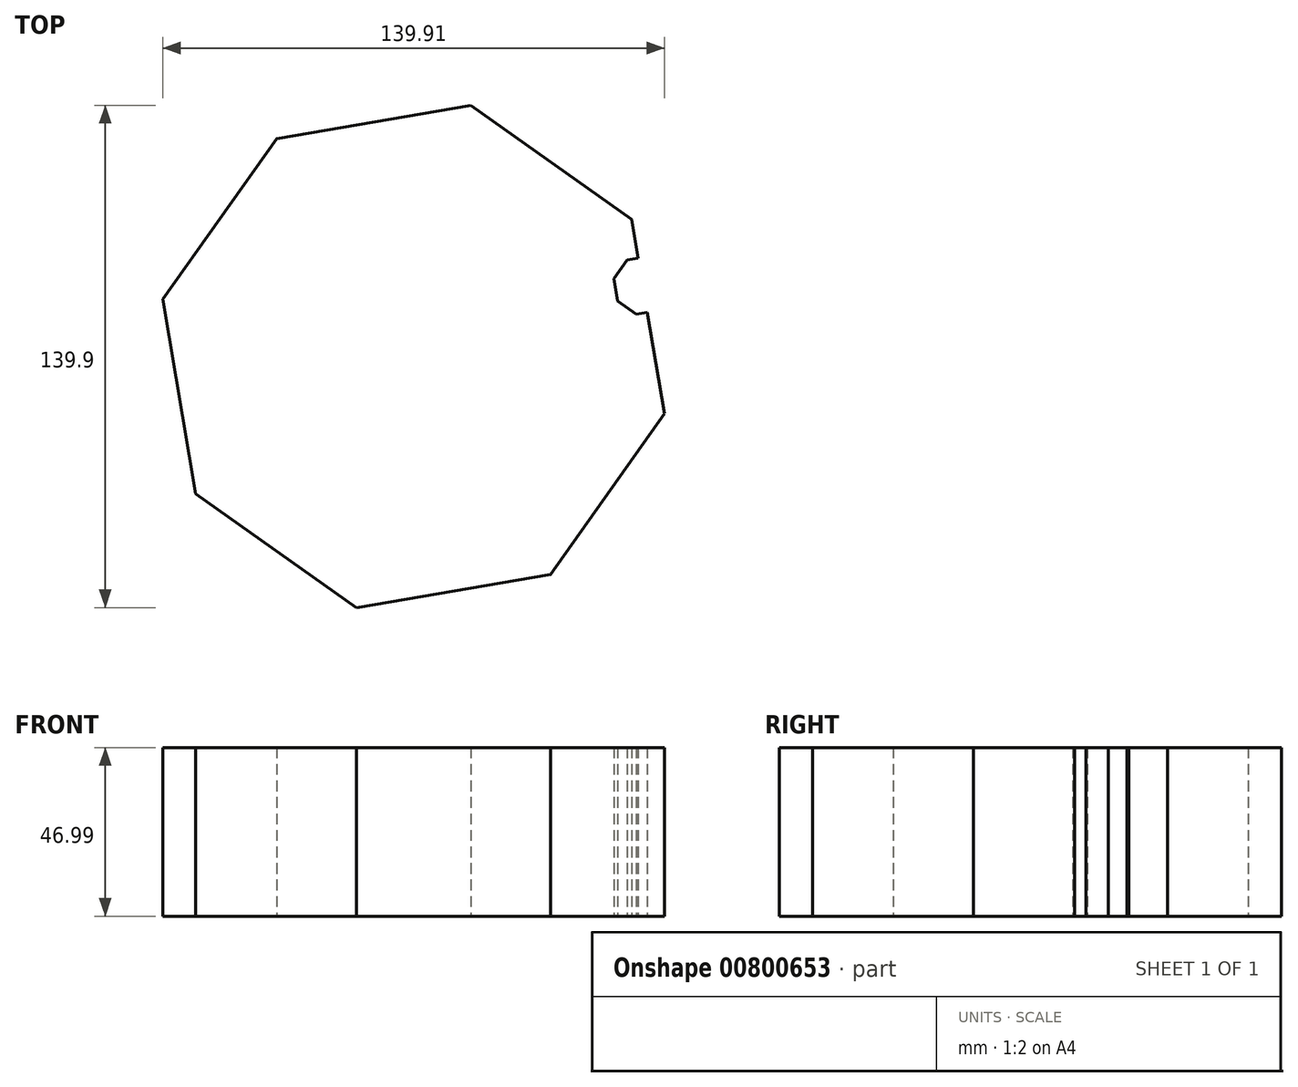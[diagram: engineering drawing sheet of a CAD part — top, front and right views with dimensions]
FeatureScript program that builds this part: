
annotation { "Feature Type Name" : "Feature", "Feature Type Description" : "" }
export const myFeature = defineFeature(function(context is Context, id is Id, definition is map)
    precondition{}
    {
        {
            var Q0;
            Q0=qCreatedBy(makeId("Top.planeOp"),FACE);
            var sketch = newSketch(context, id + "F0", { "sketchPlane" : qUnion([Q0])});
            skCircle(sketch, "E0.cCircle", {"center": v(-58.83, 0) * mm, "radius": 66.28 * mm, "construction": true});
            skLineSegment(sketch, "E0.0", {"start": v(1.9, 38.2) * mm, "end": v(11.12, -15.94) * mm});
            skLineSegment(sketch, "E0.1", {"start": v(11.12, -15.94) * mm, "end": v(-20.64, -60.73) * mm});
            skLineSegment(sketch, "E0.2", {"start": v(-20.64, -60.73) * mm, "end": v(-74.77, -69.95) * mm});
            skLineSegment(sketch, "E0.3", {"start": v(-74.77, -69.95) * mm, "end": v(-119.57, -38.2) * mm});
            skLineSegment(sketch, "E0.4", {"start": v(-119.57, -38.2) * mm, "end": v(-128.79, 15.94) * mm});
            skLineSegment(sketch, "E0.5", {"start": v(-128.79, 15.94) * mm, "end": v(-97.03, 60.73) * mm});
            skLineSegment(sketch, "E0.6", {"start": v(-97.03, 60.73) * mm, "end": v(-42.9, 69.95) * mm});
            skLineSegment(sketch, "E0.7", {"start": v(-42.9, 69.95) * mm, "end": v(1.9, 38.2) * mm});
            skPoint(sketch, "E0.0.midPoint", {"position": v(6.5, 11.13) * mm});
            skCircle(sketch, "E1.cCircle", {"center": v(5.02, 19.87) * mm, "radius": 7.65 * mm, "construction": true});
            skLineSegment(sketch, "E1.0", {"start": v(12.03, 24.28) * mm, "end": v(13.1, 18.03) * mm});
            skLineSegment(sketch, "E1.1", {"start": v(13.1, 18.03) * mm, "end": v(9.43, 12.86) * mm});
            skLineSegment(sketch, "E1.2", {"start": v(9.43, 12.86) * mm, "end": v(3.18, 11.8) * mm});
            skLineSegment(sketch, "E1.3", {"start": v(3.18, 11.8) * mm, "end": v(-2, 15.46) * mm});
            skLineSegment(sketch, "E1.4", {"start": v(-2, 15.46) * mm, "end": v(-3.06, 21.71) * mm});
            skLineSegment(sketch, "E1.5", {"start": v(-3.06, 21.71) * mm, "end": v(0.61, 26.88) * mm});
            skLineSegment(sketch, "E1.6", {"start": v(0.61, 26.88) * mm, "end": v(6.86, 27.95) * mm});
            skLineSegment(sketch, "E1.7", {"start": v(6.86, 27.95) * mm, "end": v(12.03, 24.28) * mm});
            skPoint(sketch, "E1.0.midPoint", {"position": v(12.57, 21.16) * mm});
            skSolve(sketch);
        }
        {
            var Q0;
            {var subQ7=sQuery(id+"F0.wireOp",EDGE,"E0.1");Q0=makeQuery(id+"F0.imprint","IMPRINT",FACE,{"disambiguationData":[TD([[makeQuery(id+"F0.imprint","IMPRINT",EDGE,{"derivedFrom":subQ7}),-1.0]])]});}
            extrude(context, id + "F1", {"entities" : qUnion([Q0]), "depth" : 47 * mm, "offsetDistance" : 25.4 * mm});
        }
    });
